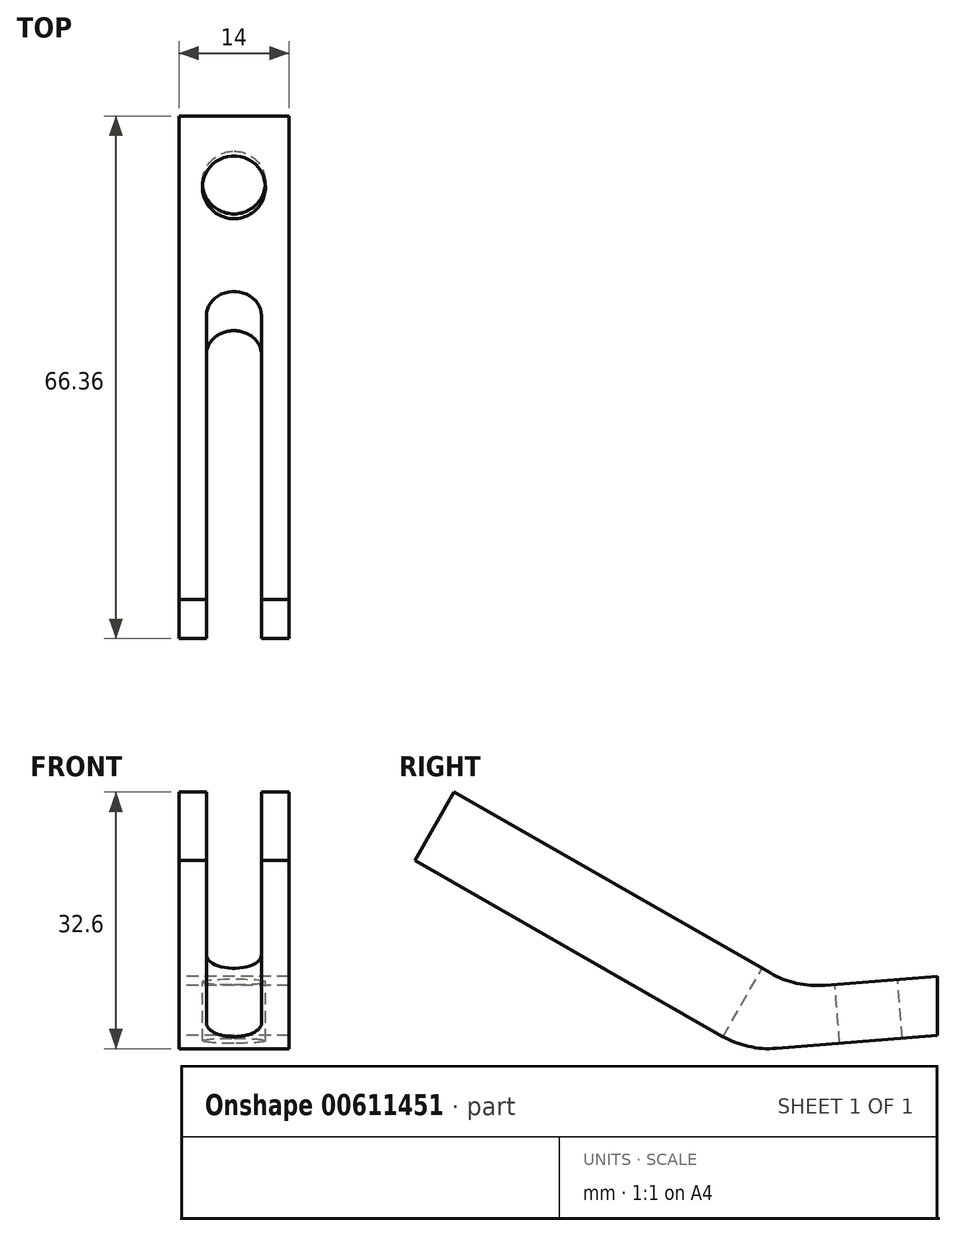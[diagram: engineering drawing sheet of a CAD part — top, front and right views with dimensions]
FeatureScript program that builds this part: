
annotation { "Feature Type Name" : "Feature", "Feature Type Description" : "" }
export const myFeature = defineFeature(function(context is Context, id is Id, definition is map)
    precondition{}
    {
        {
            var Q0;
            Q0=qCreatedBy(makeId("Right.planeOp"),FACE);
            var sketch = newSketch(context, id + "F0", { "sketchPlane" : qUnion([Q0])});
            skPoint(sketch, "E0.middle", {"position": v(0, 0) * mm});
            skLineSegment(sketch, "E1.left", {"start": v(36.39, -6.26) * mm, "end": v(36.39, -13.78) * mm, "construction": true});
            skPoint(sketch, "E2", {"position": v(0, 8.95) * mm});
            skLineSegment(sketch, "E3", {"start": v(36.39, -6.26) * mm, "end": v(36.39, -13.78) * mm});
            skPoint(sketch, "E4.orphan", {"position": v(36.63, -8.95) * mm});
            skLineSegment(sketch, "E5", {"start": v(-25, 17.14) * mm, "end": v(-29.97, 8.46) * mm});
            skLineSegment(sketch, "E6", {"start": v(-25, 17.14) * mm, "end": v(18.39, -7.7) * mm});
            skLineSegment(sketch, "E7", {"start": v(-29.97, 8.46) * mm, "end": v(12.26, -15.72) * mm});
            skLineSegment(sketch, "E8", {"start": v(36.39, -6.26) * mm, "end": v(18.39, -7.7) * mm});
            skLineSegment(sketch, "E9", {"start": v(36.39, -13.78) * mm, "end": v(12.26, -15.72) * mm});
            skLineSegment(sketch, "E10", {"start": v(-27.49, 12.8) * mm, "end": v(41.8, -26.87) * mm, "construction": true});
            skCircle(sketch, "E11", {"center": v(-22.3, 9.83) * mm, "radius": 3.1 * mm});
            skSolve(sketch);
        }
        {
            var Q0;
            Q0=makeQuery(id+"F0.imprint","IMPRINT",FACE,{"disambiguationData":[TD([[makeQuery(id+"F0.imprint","IMPRINT",EDGE,{"derivedFrom":sQuery(id+"F0.wireOp",EDGE,"E3")}),-1.0]])]});
            var Q1;
            Q1=makeQuery(id+"F0.imprint","IMPRINT",FACE,{"disambiguationData":[TD([[makeQuery(id+"F0.imprint","IMPRINT",EDGE,{"derivedFrom":sQuery(id+"F0.wireOp",EDGE,"E11")}),1.0]])]});
            extrude(context, id + "F1", {"entities" : qUnion([Q0, Q1]), "depth" : 14 * mm, "offsetDistance" : 25 * mm});
        }
        {
            var Q0;
            Q0=makeQuery(id+"F1.opExtrude","SWEPT_FACE",FACE,{"disambiguationData":[OSD([sQuery(id+"F0.wireOp",EDGE,"E8")])]});
            var sketch = newSketch(context, id + "F2", { "sketchPlane" : qUnion([Q0])});
            skLineSegment(sketch, "E12", {"start": v(7, 17.71) * mm, "end": v(7, 46.1) * mm, "construction": true});
            skCircle(sketch, "E13", {"center": v(7, 26.71) * mm, "radius": 4 * mm});
            skSolve(sketch);
        }
        {
            var Q0;
            Q0 = qSketchRegion(id + "F2", true);
            extrude(context, id + "F3", {"entities" : qUnion([Q0]), "operationType" : NewBodyOperationType.REMOVE, "oppositeDirection" : true, "depth" : 25 * mm, "offsetDistance" : 25 * mm});
        }
        {
            var Q0;
            Q0=makeQuery(id+"F1.opExtrude","SWEPT_FACE",FACE,{"disambiguationData":[OSD([sQuery(id+"F0.wireOp",EDGE,"E6")])]});
            var sketch = newSketch(context, id + "F4", { "sketchPlane" : qUnion([Q0])});
            skLineSegment(sketch, "E14", {"start": v(7, -37.55) * mm, "end": v(7, 11.36) * mm, "construction": true});
            skPoint(sketch, "E14.startSnap0", {"position": v(7, -25.21) * mm});
            skArc(sketch, "E15.0.startCap", {"start": v(10.5, -37.55) * mm, "mid": v(7, -41.05) * mm, "end": v(3.5, -37.55) * mm});
            skArc(sketch, "E15.0.endCap", {"start": v(3.5, 11.36) * mm, "mid": v(7, 14.86) * mm, "end": v(10.5, 11.36) * mm});
            skLineSegment(sketch, "E15.0.left", {"start": v(3.5, -37.55) * mm, "end": v(3.5, 11.36) * mm});
            skLineSegment(sketch, "E15.0.right", {"start": v(10.5, -37.55) * mm, "end": v(10.5, 11.36) * mm});
            skSolve(sketch);
        }
        {
            var Q0;
            Q0 = qSketchRegion(id + "F4", true);
            extrude(context, id + "F5", {"entities" : qUnion([Q0]), "operationType" : NewBodyOperationType.REMOVE, "oppositeDirection" : true, "depth" : 25 * mm, "offsetDistance" : 25 * mm});
        }
        {
            var Q0;
            Q0=makeQuery(id+"F1.opExtrude","SWEPT_EDGE",EDGE,{"disambiguationData":[OSD([sQuery(id+"F0.wireOp",EDGE,"E6"),sQuery(id+"F0.wireOp",EDGE,"E8")])]});
            var Q1;
            Q1=makeQuery(id+"F1.opExtrude","SWEPT_EDGE",EDGE,{"disambiguationData":[OSD([sQuery(id+"F0.wireOp",EDGE,"E7"),sQuery(id+"F0.wireOp",EDGE,"E9")])]});
            fillet(context, id + "F6", {"entities" : qUnion([Q0, Q1]), "radius" : 12 * mm, "tangentPropagation" : true, "allowEdgeOverflow" : false});
        }
    });
